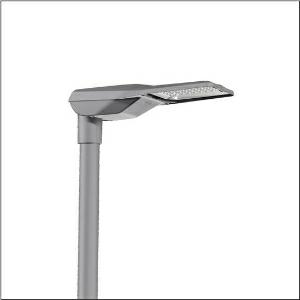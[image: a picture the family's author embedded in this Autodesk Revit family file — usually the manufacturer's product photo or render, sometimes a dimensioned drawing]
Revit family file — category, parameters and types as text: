
# Revit family: streetlight_sl_21_iq_mini___stw1_0a_5xe2e61g08hb_1142
name_source: partatom
category: Lighting Fixtures
units: mm (PartAtom-declared; Revit-internal decimal feet)

## family parameters
Cut with Voids When Loaded = No
Host = Face
Light Source = No
Part Type = Normal
Room Calculation Point = No
Round Connector Dimension = Use Diameter
Shared = No

## types (1)
- --- (1 x LED, 8480 lm, 70.9 W, 2700K)
    Apparent Load = 71 VA
    CIE Flux Codes = 38 75 98 100 100
    Color Rendering = 70
    Color Temperature = 2700K
    Default Elevation = 1800 mm
    Description = Streetlight SL 21 iQ mini, mast luminaire, primary light control with lens, of PMMA, primary optical cover: cover, of toughened safety glass, transparent, light distribution: STW1.0a, light emission: direct distribution, primary light characteristic: asymmetric, installation type: post-top, side-entry, LED, High Power LED, rated luminous flux: 8.480lm, luminous efficacy: 120lm/W, light colour: 727, colour temperature: 2700K, control gear: iQ Street-Remote, control: Street-Remote, Auto-Match, Temp-Guard, Lumen-Switch, Night-Set, Smart-Wire, Light-Fading, Desk-Remote (wireless, voltage-free reading and setting of iQ features in the workshop via application-optimized NFC function/RFID function), optimised constant luminous flux control (CLO 2.0), pre-setting: linear dimming characteristic, mains connection: 220..240V, AC, 50/60Hz, start of lifetime: 71W, end of service life: 75W, reduction: 31W, luminaire housing, of diecast aluminium, powder-coated, Siteco® metallic grey (DB 702S), corrosivity category C5 mid according to DIN EN ISO 12944, please order mast flange separately, inclination adjustable: 0°, 5°, 10°, 15°, sealing non-destructively replaceable, multi-level sealing system, length: 628mm, width: 235mm, height: 110mm, mast flange for spigot size: 42mm (side-entry): 5XC10008XM4, 60/48mm (side-entry/post-top): 5XC10108XM2, 76/60mm (side-entry/post-top): 5XC10108XM1, mounting height: 4..8m, protection rating (complete): IP66, insulation class (complete): insulation class II (safety insulation), certification: CE, ENEC, ENEC+, VDE, impact resistance: IK10, permissible operating ambient temperature for outdoor applications: -40..+50°C, standard-compliant lighting for roads and squares, packaging unit: 1 piece

Light Distribution: STW1.0a
    Height = 110 mm
    Lamp = 1 x LED
    Lamp Light Flux = 8480 lm
    Lamp Power = 70.9 W
    Lamp count = 1
    Length = 625 mm
    Luminous efficacy = 120 lm/W
    Manufacturer = Siteco
    ModVariant = No
    Model = 5XE2E61G08HB
    Number of Poles = 1
    OnlyDefault = Yes
    Power Factor = 1
    Product Name = Streetlight SL 21 iQ mini | STW1.0a
    Product group = mast luminaire | pylon top
    ProductGroupID = 6100
    Protection Class = Protection class II
    Protection Degree = IP 66
    RLX_Detail_Level = 1
    RLX_Emergency_Light_Flux = 0 lm
    RLX_Emergency_Type = 0
    RLX_Emergency_Type_DB = No
    RlxData = <blob elided: 26297 chars, md5=9f818179>
    Socket = socket
    Standby Power = 0 W
    System Light Flux = 8480 lm
    System Power = 71 W
    Type Comments = factory setting: luminous flux: 100 % | dim-lin: 254 | 711 mA
    Type Image = l_1003519.jpg
    URL = http://relux.com
    VarID = @adj_179363
    Voltage = 0 V
    Weight = 0.00 kg
    Width = 234 mm

## geometry (parser evidence)
native form markers: Blend x4, Sweep x12
no freeform markers — native parametric forms only
